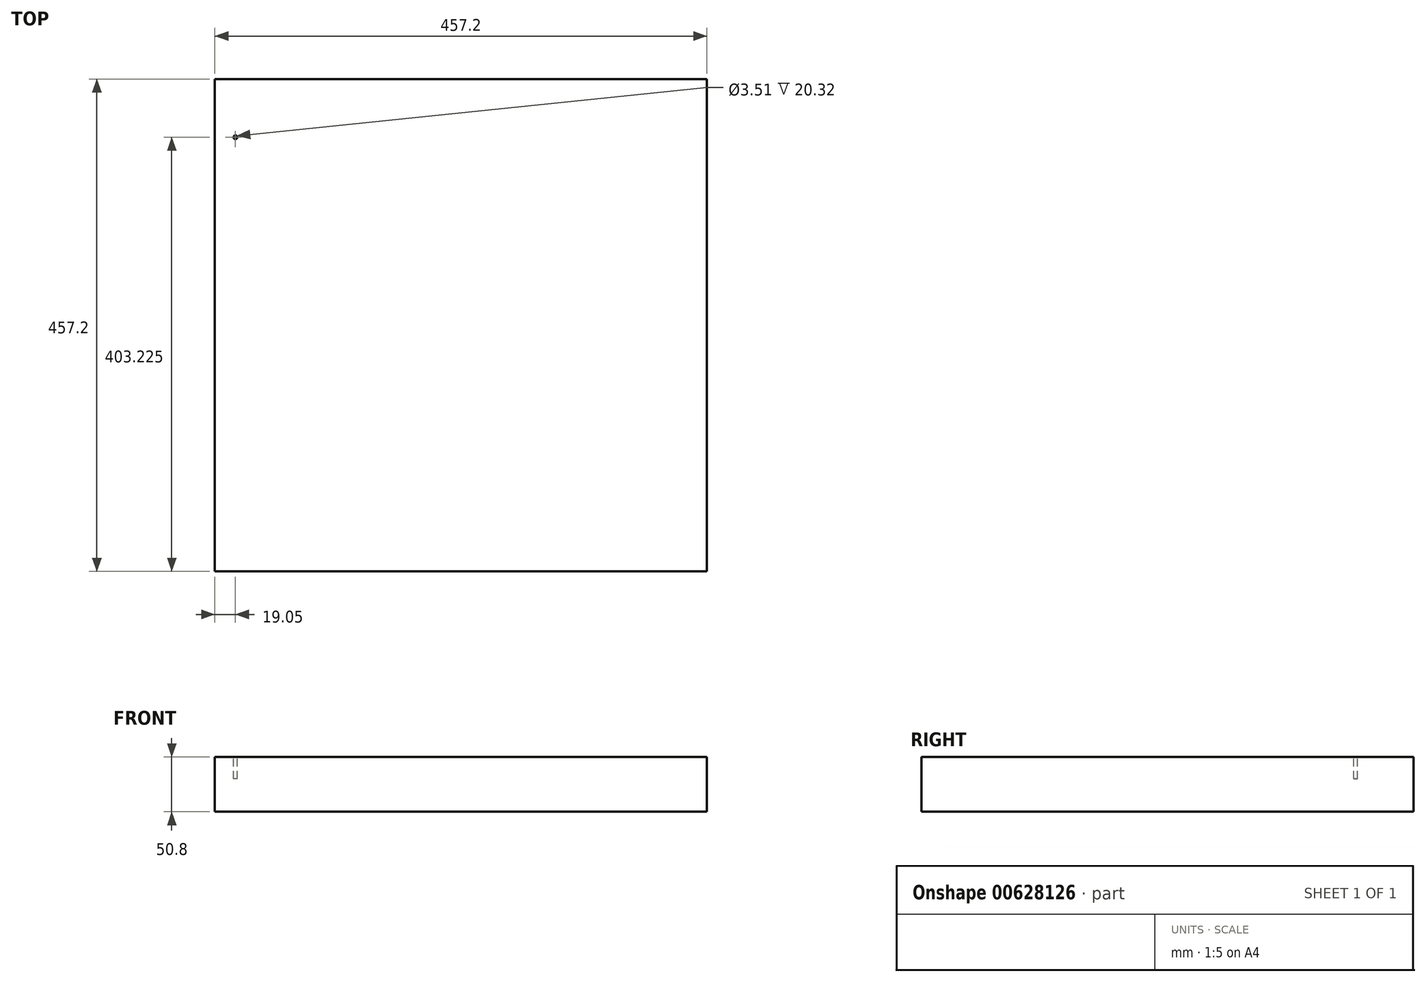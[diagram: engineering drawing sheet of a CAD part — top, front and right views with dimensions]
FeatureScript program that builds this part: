
annotation { "Feature Type Name" : "Feature", "Feature Type Description" : "" }
export const myFeature = defineFeature(function(context is Context, id is Id, definition is map)
    precondition{}
    {
        {
            var Q0;
            Q0=qCreatedBy(makeId("Top.planeOp"),FACE);
            var sketch = newSketch(context, id + "F0", { "sketchPlane" : qUnion([Q0])});
            skLineSegment(sketch, "E0.bottom", {"start": v(-228.6, -228.6) * mm, "end": v(228.6, -228.6) * mm});
            skLineSegment(sketch, "E0.top", {"start": v(-228.6, 228.6) * mm, "end": v(228.6, 228.6) * mm});
            skLineSegment(sketch, "E0.left", {"start": v(-228.6, -228.6) * mm, "end": v(-228.6, 228.6) * mm});
            skLineSegment(sketch, "E0.right", {"start": v(228.6, -228.6) * mm, "end": v(228.6, 228.6) * mm});
            skPoint(sketch, "E0.middle", {"position": v(0, 0) * mm});
            skSolve(sketch);
        }
        {
            var Q0;
            Q0=makeQuery(id+"F0.imprint","IMPRINT",FACE,{"disambiguationData":[TD([[makeQuery(id+"F0.imprint","IMPRINT",EDGE,{"derivedFrom":sQuery(id+"F0.wireOp",EDGE,"E0.bottom")}),1.0]])]});
            extrude(context, id + "F1", {"entities" : qUnion([Q0]), "depth" : 50.8 * mm, "offsetDistance" : 25.4 * mm});
        }
        {
            var Q0;
            Q0=makeQuery(id+"F1.opExtrude","CAP_FACE",FACE,{"disambiguationData":[OSD([sQuery(id+"F0.wireOp",EDGE,"E0.bottom"),sQuery(id+"F0.wireOp",EDGE,"E0.top"),sQuery(id+"F0.wireOp",EDGE,"E0.left"),sQuery(id+"F0.wireOp",EDGE,"E0.right")])],"isStart":false});
            var sketch = newSketch(context, id + "F2", { "sketchPlane" : qUnion([Q0])});
            skCircle(sketch, "E1", {"center": v(-209.55, 209.55) * mm, "radius": 19.05 * mm, "construction": true});
            skLineSegment(sketch, "E2", {"start": v(0, 0) * mm, "end": v(0, 228.6) * mm, "construction": true});
            skLineSegment(sketch, "E3", {"start": v(0, 0) * mm, "end": v(-228.6, 0) * mm, "construction": true});
            skLineSegment(sketch, "E4", {"start": v(-209.55, 209.55) * mm, "end": v(-209.55, 174.63) * mm, "construction": true});
            skCircle(sketch, "E5", {"center": v(-209.55, 174.63) * mm, "radius": 1.75 * mm});
            skSolve(sketch);
        }
        {
            var Q0;
            Q0=makeQuery(id+"F2.imprint","IMPRINT",FACE,{"disambiguationData":[TD([[makeQuery(id+"F2.imprint","IMPRINT",EDGE,{"derivedFrom":sQuery(id+"F2.wireOp",EDGE,"E5")}),1.0]])]});
            extrude(context, id + "F3", {"entities" : qUnion([Q0]), "operationType" : NewBodyOperationType.REMOVE, "oppositeDirection" : true, "depth" : 20.32 * mm, "offsetDistance" : 25.4 * mm});
        }
    });
